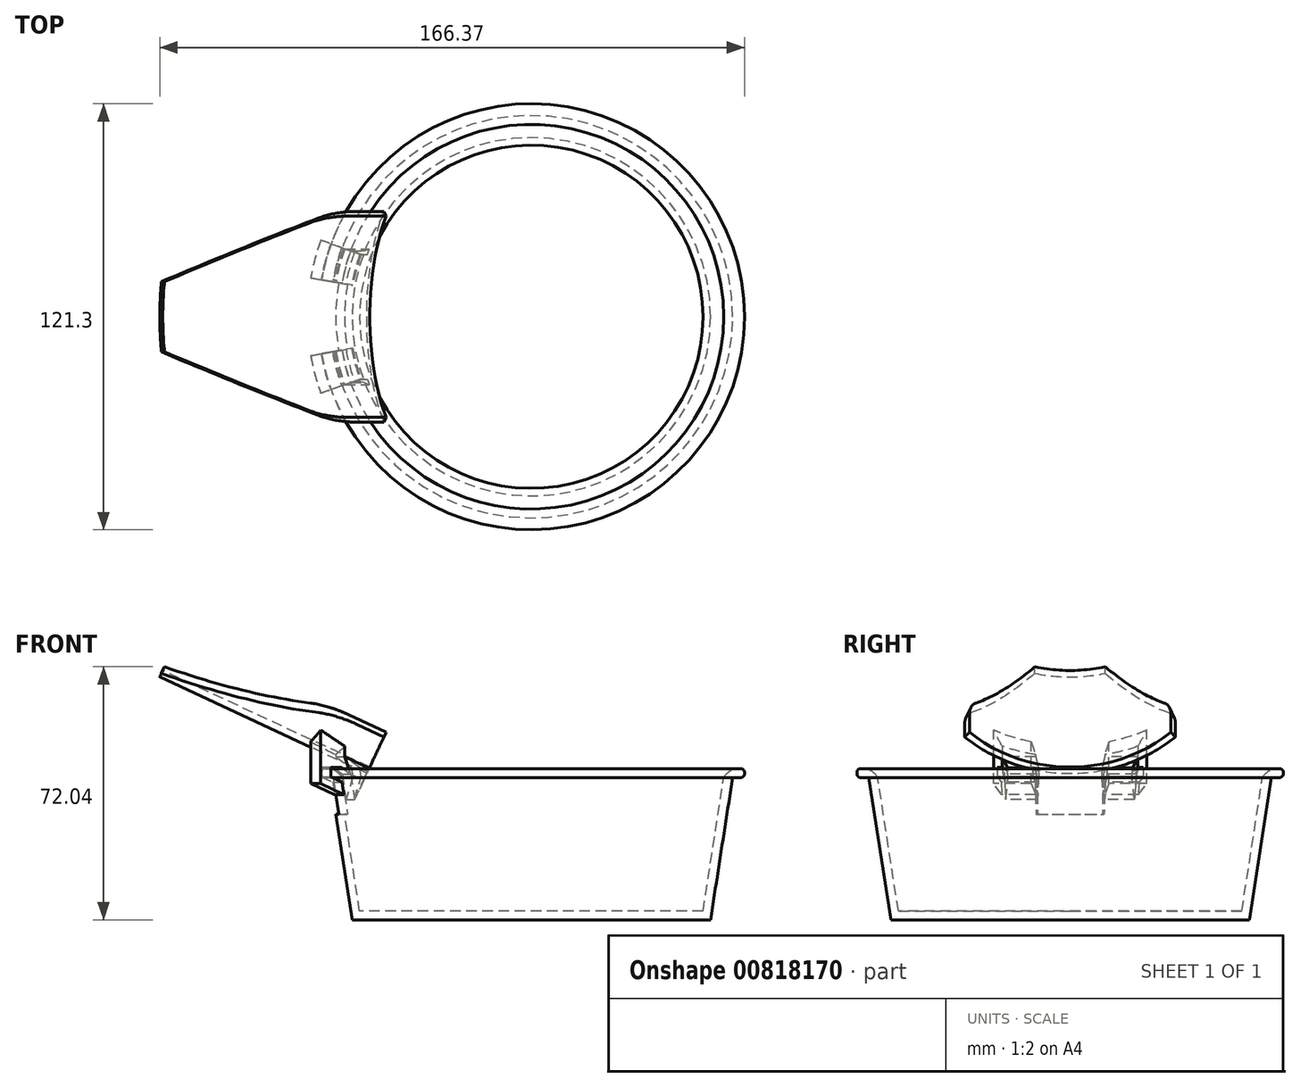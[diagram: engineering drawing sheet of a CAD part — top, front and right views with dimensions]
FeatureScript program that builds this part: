
annotation { "Feature Type Name" : "Feature", "Feature Type Description" : "" }
export const myFeature = defineFeature(function(context is Context, id is Id, definition is map)
    precondition{}
    {
        {
            var Q0;
            Q0=qCreatedBy(makeId("Front.planeOp"),FACE);
            var sketch = newSketch(context, id + "F0", { "sketchPlane" : qUnion([Q0])});
            skLineSegment(sketch, "E0", {"start": v(0, 0) * mm, "end": v(0, 46.12) * mm, "construction": true});
            skSolve(sketch);
        }
        {
            var Q0;
            Q0=qCreatedBy(makeId("Top.planeOp"),FACE);
            var sketch = newSketch(context, id + "F1", { "sketchPlane" : qUnion([Q0])});
            skCircle(sketch, "E1", {"center": v(0, 0) * mm, "radius": 51 * mm});
            skSolve(sketch);
        }
        {
            var Q0;
            Q0=qCreatedBy(makeId("Top.planeOp"),FACE);
            cPlane(context, id + "F2", {"entities" : qUnion([Q0]), "cplaneType" : CPlaneType.OFFSET, "offset" : 40.5 * mm, "width" : 150 * mm, "height" : 150 * mm});
        }
        {
            var Q0;
            Q0=qCreatedBy(id+"F2.planeOp",FACE);
            var sketch = newSketch(context, id + "F3", { "sketchPlane" : qUnion([Q0])});
            skCircle(sketch, "E2", {"center": v(0, 0) * mm, "radius": 57.27 * mm});
            skSolve(sketch);
        }
        {
            var Q0;
            Q0=makeQuery(id+"F1.imprint","IMPRINT",FACE,{"disambiguationData":[TD([[makeQuery(id+"F1.imprint","IMPRINT",EDGE,{"derivedFrom":sQuery(id+"F1.wireOp",EDGE,"E1")}),1.0]])]});
            var Q1;
            Q1=makeQuery(id+"F3.imprint","IMPRINT",FACE,{"disambiguationData":[TD([[makeQuery(id+"F3.imprint","IMPRINT",EDGE,{"derivedFrom":sQuery(id+"F3.wireOp",EDGE,"E2")}),1.0]])]});
            loft(context, id + "F4", {"sheetProfilesArray" : [{ "sheetProfileEntities" : qUnion([Q0]) }, { "sheetProfileEntities" : qUnion([Q1]) }]});
        }
        {
            var Q0;
            Q0=makeQuery(id+"F4.opLoft","CAP_FACE",FACE,{"disambiguationData":[OSD([makeQuery(id+"F3.imprint","IMPRINT",FACE,{"disambiguationData":[TD([[makeQuery(id+"F3.imprint","IMPRINT",EDGE,{"derivedFrom":sQuery(id+"F3.wireOp",EDGE,"E2")}),1.0]])]})])],"isStart":true});
            var sketch = newSketch(context, id + "F5", { "sketchPlane" : qUnion([Q0])});
            skCircle(sketch, "E3", {"center": v(0, 0) * mm, "radius": 60.65 * mm});
            skSolve(sketch);
        }
        {
            var Q0;
            Q0=makeQuery(id+"F4.opLoft","CAP_FACE",FACE,{"disambiguationData":[OSD([makeQuery(id+"F3.imprint","IMPRINT",FACE,{"disambiguationData":[TD([[makeQuery(id+"F3.imprint","IMPRINT",EDGE,{"derivedFrom":sQuery(id+"F3.wireOp",EDGE,"E2")}),1.0]])]})])],"isStart":true});
            shell(context, id + "F6", {"entities" : qUnion([Q0]), "thickness" : 2.5 * mm});
        }
        {
            var Q0;
            Q0=makeQuery(id+"F5.imprint","IMPRINT",FACE,{"disambiguationData":[TD([[makeQuery(id+"F5.imprint","IMPRINT",EDGE,{"derivedFrom":sQuery(id+"F5.wireOp",EDGE,"E3")}),1.0]])]});
            var Q1;
            Q1=makeQuery(id+"F4.opLoft","CAP_FACE",FACE,{"disambiguationData":[OSD([makeQuery(id+"F3.imprint","IMPRINT",FACE,{"disambiguationData":[TD([[makeQuery(id+"F3.imprint","IMPRINT",EDGE,{"derivedFrom":sQuery(id+"F3.wireOp",EDGE,"E2")}),1.0]])]})])],"isStart":true});
            extrude(context, id + "F7", {"entities" : qUnion([Q0, Q1]), "operationType" : NewBodyOperationType.ADD, "depth" : 2.55 * mm, "offsetDistance" : 25 * mm});
        }
        {
            var Q0;
            Q0=makeQuery(id+"F7.opExtrude","CAP_EDGE",EDGE,{"disambiguationData":[OSD([sQuery(id+"F5.wireOp",EDGE,"E3")])],"isStart":false});
            var Q1;
            Q1=makeQuery(id+"F7.opExtrude","CAP_EDGE",EDGE,{"disambiguationData":[OSD([sQuery(id+"F5.wireOp",EDGE,"E3")])],"isStart":true});
            fillet(context, id + "F8", {"entities" : qUnion([Q0, Q1]), "radius" : 1 * mm, "tangentPropagation" : true, "allowEdgeOverflow" : false});
        }
        {
            var Q0;
            {var subQ0=sQuery(id+"F3.wireOp",EDGE,"E2");Q0=makeQuery(id+"F7.opExtrude","CAP_EDGE",EDGE,{"disambiguationData":[OSD([subQ0]),TDD([makeQuery(id+"F6.opShell","OFFSET_EDGE",EDGE,{"disambiguationData":[OSD([subQ0])]})])],"isStart":false});}
            fillet(context, id + "F9", {"entities" : qUnion([Q0]), "radius" : 5 * mm, "tangentPropagation" : true, "allowEdgeOverflow" : false});
        }
        {
            var Q0;
            Q0=qCreatedBy(makeId("Front.planeOp"),FACE);
            var sketch = newSketch(context, id + "F10", { "sketchPlane" : qUnion([Q0])});
            skLineSegment(sketch, "E4", {"start": v(-57.38, 39.2) * mm, "end": v(-56.83, 35.67) * mm});
            skLineSegment(sketch, "E5", {"start": v(-56.83, 35.67) * mm, "end": v(-63.75, 38.75) * mm});
            skLineSegment(sketch, "E6", {"start": v(-63.75, 38.75) * mm, "end": v(-63.75, 46.4) * mm});
            skLineSegment(sketch, "E7", {"start": v(-63.75, 46.4) * mm, "end": v(-60.75, 46.4) * mm});
            skLineSegment(sketch, "E8", {"start": v(-60.75, 46.4) * mm, "end": v(-60.75, 40.7) * mm});
            skLineSegment(sketch, "E9", {"start": v(-60.75, 40.7) * mm, "end": v(-57.38, 39.2) * mm});
            skLineSegment(sketch, "E10", {"start": v(-60.75, 43.4) * mm, "end": v(-57.45, 43.4) * mm});
            skLineSegment(sketch, "E11", {"start": v(-57.45, 43.4) * mm, "end": v(-54.7, 41.5) * mm});
            skLineSegment(sketch, "E12", {"start": v(-54.7, 41.5) * mm, "end": v(-53.57, 34.22) * mm});
            skLineSegment(sketch, "E13", {"start": v(-53.57, 34.22) * mm, "end": v(-51.55, 40.76) * mm});
            skLineSegment(sketch, "E14", {"start": v(-51.55, 40.76) * mm, "end": v(-51.93, 43.23) * mm});
            skLineSegment(sketch, "E15", {"start": v(-51.93, 43.23) * mm, "end": v(-56.5, 46.4) * mm});
            skLineSegment(sketch, "E16", {"start": v(-56.5, 46.4) * mm, "end": v(-60.75, 46.4) * mm});
            skLineSegment(sketch, "E17", {"start": v(-48.86, 2.5) * mm, "end": v(-54.75, 40.5) * mm, "construction": true});
            skSolve(sketch);
        }
        {
            var Q0;
            Q0 = qSketchRegion(id + "F10", true);
            var Q1;
            Q1=sQuery(id+"F0.wireOp",EDGE,"E0");
            revolve(context, id + "F11", {"surfaceOperationType" : NewSurfaceOperationType.NEW, "entities" : qUnion([Q0]), "axis" : qUnion([Q1]), "revolveType" : RevolveType.SYMMETRIC, "oppositeDirection" : true, "angle" : 40 * degree});
        }
        {
            var Q0;
            Q0=qCreatedBy(makeId("Front.planeOp"),FACE);
            var sketch = newSketch(context, id + "F12", { "sketchPlane" : qUnion([Q0])});
            skLineSegment(sketch, "E18.bottom", {"start": v(-70, 50) * mm, "end": v(-40, 50) * mm});
            skLineSegment(sketch, "E18.top", {"start": v(-70, 30) * mm, "end": v(-40, 30) * mm});
            skLineSegment(sketch, "E18.left", {"start": v(-70, 50) * mm, "end": v(-70, 30) * mm});
            skLineSegment(sketch, "E18.right", {"start": v(-40, 50) * mm, "end": v(-40, 30) * mm});
            skSolve(sketch);
        }
        {
            var Q0;
            Q0 = qSketchRegion(id + "F12", true);
            var Q1;
            Q1=sQuery(id+"F0.wireOp",EDGE,"E0");
            revolve(context, id + "F13", {"operationType" : NewBodyOperationType.REMOVE, "surfaceOperationType" : NewSurfaceOperationType.NEW, "entities" : qUnion([Q0]), "axis" : qUnion([Q1]), "revolveType" : RevolveType.SYMMETRIC, "oppositeDirection" : true, "angle" : 20 * degree});
        }
        {
            var Q0;
            {var subQ0=sQuery(id+"F10.wireOp",EDGE,"E16");var subQ2=sQuery(id+"F10.wireOp",EDGE,"E7");Q0=makeQuery(id+"F13.boolean.opBoolean","SPLIT",FACE,{"disambiguationData":[TD([makeQuery(id+"F13.opRevolve","CAP_FACE",FACE,{"disambiguationData":[OSD([sQuery(id+"F12.wireOp",EDGE,"E18.bottom"),sQuery(id+"F12.wireOp",EDGE,"E18.top"),sQuery(id+"F12.wireOp",EDGE,"E18.left"),sQuery(id+"F12.wireOp",EDGE,"E18.right")])],"isStart":false})])],"derivedFrom":makeQuery(id+"F11.opRevolve","SWEPT_FACE",FACE,{"disambiguationData":[OSD([subQ2,subQ0])]})});}
            var sketch = newSketch(context, id + "F14", { "sketchPlane" : qUnion([Q0])});
            skLineSegment(sketch, "E19", {"start": v(-55.65, 9.81) * mm, "end": v(-55.65, -9.81) * mm, "construction": true});
            skSolve(sketch);
        }
        {
            var Q0;
            Q0=sQuery(id+"F14.wireOp",EDGE,"E19");
            cPlane(context, id + "F15", {"entities" : qUnion([Q0]), "cplaneType" : CPlaneType.LINE_ANGLE, "offset" : 25 * mm, "angle" : 65 * degree, "width" : 150 * mm, "height" : 150 * mm});
        }
        {
            var Q0;
            Q0=qCreatedBy(id+"F15.planeOp",FACE);
            var sketch = newSketch(context, id + "F16", { "sketchPlane" : qUnion([Q0])});
            skCircle(sketch, "E20", {"center": v(0, 63) * mm, "radius": 45 * mm});
            skCircle(sketch, "E21", {"center": v(0, 63) * mm, "radius": 43 * mm});
            skLineSegment(sketch, "E22", {"start": v(0, 63) * mm, "end": v(-30, 29.46) * mm});
            skLineSegment(sketch, "E23", {"start": v(0, 63) * mm, "end": v(30, 29.46) * mm});
            skSolve(sketch);
        }
        {
            var Q0;
            {var subQ0=sQuery(id+"F16.wireOp",EDGE,"E22");var subQ1=sQuery(id+"F16.wireOp",EDGE,"E20");var subQ2=makeQuery(id+"F16.imprint","INTERSECT",VERTEX,{"derivedFrom":[subQ1,subQ0]});Q0=makeQuery(id+"F16.imprint","IMPRINT",FACE,{"disambiguationData":[TD([[makeQuery(id+"F16.imprint","IMPRINT",EDGE,{"disambiguationData":[TD([[subQ2,-1.0]])],"derivedFrom":subQ1}),1.0]])]});}
            extrude(context, id + "F17", {"entities" : qUnion([Q0]), "depth" : 10 * mm, "offsetDistance" : 25 * mm, "hasSecondDirection" : true, "secondDirectionOppositeDirection" : true, "secondDirectionDepth" : 55 * mm});
        }
        {
            var Q0;
            {var subQ0=sQuery(id+"F10.wireOp",EDGE,"E16");var subQ2=sQuery(id+"F10.wireOp",EDGE,"E7");Q0=makeQuery(id+"F13.boolean.opBoolean","SPLIT",FACE,{"disambiguationData":[TD([makeQuery(id+"F13.opRevolve","CAP_FACE",FACE,{"disambiguationData":[OSD([sQuery(id+"F12.wireOp",EDGE,"E18.bottom"),sQuery(id+"F12.wireOp",EDGE,"E18.top"),sQuery(id+"F12.wireOp",EDGE,"E18.left"),sQuery(id+"F12.wireOp",EDGE,"E18.right")])],"isStart":true})])],"derivedFrom":makeQuery(id+"F11.opRevolve","SWEPT_FACE",FACE,{"disambiguationData":[OSD([subQ2,subQ0])]})});}
            var Q1;
            {var subQ0=sQuery(id+"F10.wireOp",EDGE,"E16");var subQ1=sQuery(id+"F10.wireOp",EDGE,"E7");Q1=makeQuery(id+"F14.imprint","IMPRINT",FACE,{"disambiguationData":[TD([[makeQuery(id+"F14.imprint","IMPRINT",EDGE,{"derivedFrom":makeQuery(id+"F11.opRevolve","CAP_EDGE",EDGE,{"disambiguationData":[OSD([subQ1,subQ0])],"isStart":false})}),-1.0]])]});}
            var Q2;
            Q2=makeQuery(id+"F17.opExtrude","SWEPT_BODY",BODY,{"disambiguationData":[OSD([sQuery(id+"F16.wireOp",EDGE,"E20"),sQuery(id+"F16.wireOp",EDGE,"E21"),sQuery(id+"F16.wireOp",EDGE,"E22"),sQuery(id+"F16.wireOp",EDGE,"E23")])]});
            extrude(context, id + "F18", {"entities" : qUnion([Q0, Q1]), "operationType" : NewBodyOperationType.ADD, "endBound" : BoundingType.UP_TO_BODY, "depth" : 25 * mm, "endBoundEntityBody" : qUnion([Q2]), "offsetDistance" : 25 * mm});
        }
        {
            var Q0;
            Q0=makeQuery(id+"F17.opExtrude","CAP_VERTEX",VERTEX,{"disambiguationData":[OSD([sQuery(id+"F16.wireOp",EDGE,"E21"),sQuery(id+"F16.wireOp",EDGE,"E23")])],"isStart":true});
            var Q1;
            Q1=makeQuery(id+"F17.opExtrude","CAP_VERTEX",VERTEX,{"disambiguationData":[OSD([sQuery(id+"F16.wireOp",EDGE,"E21"),sQuery(id+"F16.wireOp",EDGE,"E22")])],"isStart":true});
            var Q2;
            Q2=makeQuery(id+"F17.opExtrude","CAP_VERTEX",VERTEX,{"disambiguationData":[OSD([sQuery(id+"F16.wireOp",EDGE,"E21"),sQuery(id+"F16.wireOp",EDGE,"E22")])],"isStart":false});
            cPlane(context, id + "F19", {"entities" : qUnion([Q0, Q1, Q2]), "cplaneType" : CPlaneType.THREE_POINT, "offset" : 25 * mm, "width" : 150 * mm, "height" : 150 * mm});
        }
        {
            var Q0;
            Q0=qCreatedBy(id+"F19.planeOp",FACE);
            var sketch = newSketch(context, id + "F20", { "sketchPlane" : qUnion([Q0])});
            skLineSegment(sketch, "E24", {"start": v(-125.05, 0) * mm, "end": v(-56.5, 0) * mm, "construction": true});
            skLineSegment(sketch, "E25", {"start": v(-125.05, 10) * mm, "end": v(-75.05, 30) * mm});
            skLineSegment(sketch, "E26", {"start": v(-75.05, 30) * mm, "end": v(-125.05, 30) * mm});
            skLineSegment(sketch, "E27", {"start": v(-125.05, 30) * mm, "end": v(-125.05, 10) * mm});
            skLineSegment(sketch, "E28.MirrorCS", {"start": v(-125.05, -10) * mm, "end": v(-75.05, -30) * mm});
            skLineSegment(sketch, "E29.MirrorCS", {"start": v(-125.05, -30) * mm, "end": v(-125.05, -10) * mm});
            skLineSegment(sketch, "E30.MirrorCS", {"start": v(-75.05, -30) * mm, "end": v(-125.05, -30) * mm});
            skSolve(sketch);
        }
        {
            var Q0;
            Q0=makeQuery(id+"F20.imprint","IMPRINT",FACE,{"disambiguationData":[TD([[makeQuery(id+"F20.imprint","IMPRINT",EDGE,{"derivedFrom":sQuery(id+"F20.wireOp",EDGE,"E25")}),1.0]])]});
            var Q1;
            Q1=makeQuery(id+"F20.imprint","IMPRINT",FACE,{"disambiguationData":[TD([[makeQuery(id+"F20.imprint","IMPRINT",EDGE,{"derivedFrom":sQuery(id+"F20.wireOp",EDGE,"E28.MirrorCS")}),-1.0]])]});
            extrude(context, id + "F21", {"entities" : qUnion([Q0, Q1]), "operationType" : NewBodyOperationType.REMOVE, "endBound" : BoundingType.THROUGH_ALL, "depth" : 25 * mm, "offsetDistance" : 25 * mm});
        }
        {
            var Q0;
            Q0=makeQuery(id+"F21.boolean.opBoolean","COPY",EDGE,{"derivedFrom":makeQuery(id+"F21.opExtrude","SWEPT_EDGE",EDGE,{"disambiguationData":[OSD([sQuery(id+"F20.wireOp",EDGE,"E25"),sQuery(id+"F20.wireOp",EDGE,"E27")])]})});
            var Q1;
            Q1=makeQuery(id+"F21.boolean.opBoolean","COPY",EDGE,{"derivedFrom":makeQuery(id+"F21.opExtrude","SWEPT_EDGE",EDGE,{"disambiguationData":[OSD([sQuery(id+"F20.wireOp",EDGE,"E28.MirrorCS"),sQuery(id+"F20.wireOp",EDGE,"E29.MirrorCS")])]})});
            var Q2;
            Q2=makeQuery(id+"F21.boolean.opBoolean","INTERSECT",EDGE,{"derivedFrom":[makeQuery(id+"F17.opExtrude","SWEPT_FACE",FACE,{"disambiguationData":[OSD([sQuery(id+"F16.wireOp",EDGE,"E22")])]}),makeQuery(id+"F21.opExtrude","SWEPT_FACE",FACE,{"disambiguationData":[OSD([sQuery(id+"F20.wireOp",EDGE,"E25")])]})]});
            var Q3;
            Q3=makeQuery(id+"F21.boolean.opBoolean","INTERSECT",EDGE,{"derivedFrom":[makeQuery(id+"F17.opExtrude","SWEPT_FACE",FACE,{"disambiguationData":[OSD([sQuery(id+"F16.wireOp",EDGE,"E23")])]}),makeQuery(id+"F21.opExtrude","SWEPT_FACE",FACE,{"disambiguationData":[OSD([sQuery(id+"F20.wireOp",EDGE,"E28.MirrorCS")])]})]});
            fillet(context, id + "F22", {"entities" : qUnion([Q0, Q1, Q2, Q3]), "radius" : 8 * mm, "tangentPropagation" : true, "allowEdgeOverflow" : false});
        }
        {
            var Q0;
            Q0=makeQuery(id+"F17.opExtrude","CAP_FACE",FACE,{"disambiguationData":[OSD([sQuery(id+"F16.wireOp",EDGE,"E20"),sQuery(id+"F16.wireOp",EDGE,"E21"),sQuery(id+"F16.wireOp",EDGE,"E22"),sQuery(id+"F16.wireOp",EDGE,"E23")])],"isStart":false});
            var sketch = newSketch(context, id + "F23", { "sketchPlane" : qUnion([Q0])});
            skArc(sketch, "E31.0", {"start": v(-30, 29.46) * mm, "mid": v(0, 18) * mm, "end": v(30, 29.46) * mm});
            skLineSegment(sketch, "E31.1", {"start": v(-19.33, 22.36) * mm, "end": v(-19.33, 19.61) * mm});
            skLineSegment(sketch, "E31.2", {"start": v(-17.76, 18.56) * mm, "end": v(-19.33, 19.61) * mm});
            skLineSegment(sketch, "E31.3", {"start": v(-17.63, 16.47) * mm, "end": v(-17.76, 18.56) * mm});
            skLineSegment(sketch, "E31.4", {"start": v(-18.32, 9.74) * mm, "end": v(-17.63, 16.47) * mm});
            skEllipticalArc(sketch, "E31.5", {});
            skLineSegment(sketch, "E31.6", {"start": v(-8.95, 15.5) * mm, "end": v(-9.3, 8.72) * mm});
            skLineSegment(sketch, "E31.7", {"start": v(-9.02, 17.57) * mm, "end": v(-8.95, 15.5) * mm});
            skLineSegment(sketch, "E31.8", {"start": v(-9.81, 18.53) * mm, "end": v(-9.02, 17.57) * mm});
            skLineSegment(sketch, "E31.9", {"start": v(-9.81, 19.08) * mm, "end": v(-9.81, 18.53) * mm});
            skLineSegment(sketch, "E31.10", {"start": v(8.95, 15.5) * mm, "end": v(9.3, 8.72) * mm});
            skLineSegment(sketch, "E31.11", {"start": v(9.02, 17.57) * mm, "end": v(8.95, 15.5) * mm});
            skLineSegment(sketch, "E31.12", {"start": v(9.81, 18.53) * mm, "end": v(9.02, 17.57) * mm});
            skLineSegment(sketch, "E31.13", {"start": v(9.81, 19.08) * mm, "end": v(9.81, 18.53) * mm});
            skEllipticalArc(sketch, "E31.14", {});
            skLineSegment(sketch, "E31.15", {"start": v(18.32, 9.74) * mm, "end": v(17.63, 16.47) * mm});
            skLineSegment(sketch, "E31.16", {"start": v(17.63, 16.47) * mm, "end": v(17.76, 18.56) * mm});
            skLineSegment(sketch, "E31.17", {"start": v(17.76, 18.56) * mm, "end": v(19.33, 19.61) * mm});
            skLineSegment(sketch, "E31.18", {"start": v(19.33, 22.36) * mm, "end": v(19.33, 19.61) * mm});
            skLineSegment(sketch, "E32.0", {"start": v(-18.7, 15.89) * mm, "end": v(-18.32, 9.74) * mm});
            skLineSegment(sketch, "E32.1", {"start": v(18.7, 15.89) * mm, "end": v(18.32, 9.74) * mm});
            skLineSegment(sketch, "E33", {"start": v(-18.7, 15.89) * mm, "end": v(-19.33, 19.61) * mm});
            skLineSegment(sketch, "E34", {"start": v(18.7, 15.89) * mm, "end": v(19.33, 19.61) * mm});
            const initialGuessF23  = {"E31.5": [0, 0.03162733839321066, 1, 0, 0.053674650700035235, 0.022683887578388108, 4.363323129985824, 4.537856055185257], "E31.14": [0, 0.03162733839321066, 1, 0, 0.053674650700035235, 0.022683887578388108, 4.886921905584122, 5.061454830783555]};
            skSetInitialGuess(sketch, initialGuessF23);
            skSolve(sketch);
        }
        {
            var Q0;
            Q0 = qSketchRegion(id + "F23", true);
            var Q1;
            Q1=makeQuery(id+"F13.boolean.opBoolean","SPLIT",BODY,{"disambiguationData":[OD(0.0)],"derivedFrom":makeQuery(id+"F11.opRevolve","SWEPT_BODY",BODY,{"disambiguationData":[OSD([sQuery(id+"F10.wireOp",EDGE,"E4"),sQuery(id+"F10.wireOp",EDGE,"E5"),sQuery(id+"F10.wireOp",EDGE,"E6"),sQuery(id+"F10.wireOp",EDGE,"E7"),sQuery(id+"F10.wireOp",EDGE,"E8"),sQuery(id+"F10.wireOp",EDGE,"E9"),sQuery(id+"F10.wireOp",EDGE,"E10"),sQuery(id+"F10.wireOp",EDGE,"E11"),sQuery(id+"F10.wireOp",EDGE,"E12"),sQuery(id+"F10.wireOp",EDGE,"E13"),sQuery(id+"F10.wireOp",EDGE,"E14"),sQuery(id+"F10.wireOp",EDGE,"E15"),sQuery(id+"F10.wireOp",EDGE,"E16")])]})});
            extrude(context, id + "F24", {"entities" : qUnion([Q0]), "operationType" : NewBodyOperationType.ADD, "endBound" : BoundingType.UP_TO_BODY, "oppositeDirection" : true, "depth" : 25 * mm, "endBoundEntityBody" : qUnion([Q1]), "offsetDistance" : 25 * mm});
        }
    });
